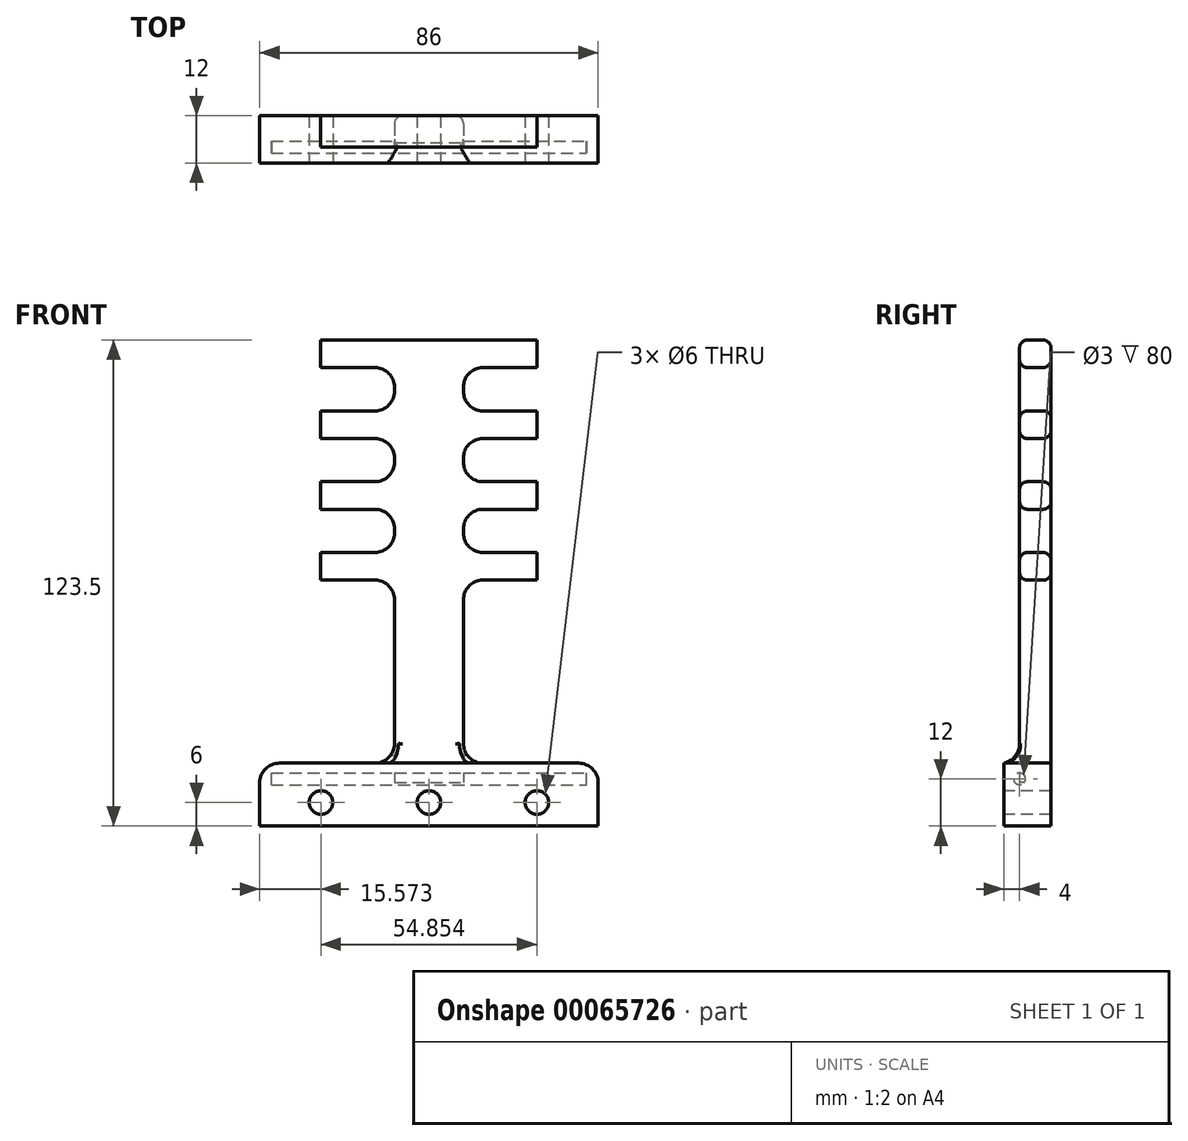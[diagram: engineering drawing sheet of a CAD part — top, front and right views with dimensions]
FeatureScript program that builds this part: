
annotation { "Feature Type Name" : "Feature", "Feature Type Description" : "" }
export const myFeature = defineFeature(function(context is Context, id is Id, definition is map)
    precondition{}
    {
        {
            var Q0;
            Q0=qCreatedBy(makeId("Top.planeOp"),FACE);
            var sketch = newSketch(context, id + "F0", { "sketchPlane" : qUnion([Q0])});
            skPoint(sketch, "E0.rect.middle", {"position": v(0, 0) * mm});
            skLineSegment(sketch, "E1", {"start": v(0, 0) * mm, "end": v(0, 2) * mm});
            skLineSegment(sketch, "E2", {"start": v(0, 2) * mm, "end": v(12, 2) * mm, "construction": true});
            skCircle(sketch, "E3", {"center": v(12, 2) * mm, "radius": 3 * mm});
            skCircle(sketch, "E4", {"center": v(12, 2) * mm, "radius": 6 * mm});
            skCircle(sketch, "E5.MirrorC", {"center": v(-12, 2) * mm, "radius": 3 * mm});
            skCircle(sketch, "E6.MirrorC", {"center": v(-12, 2) * mm, "radius": 6 * mm});
            skPoint(sketch, "E7.rect.middle", {"position": v(0, 2) * mm});
            skLineSegment(sketch, "E8", {"start": v(35, -4) * mm, "end": v(20.22, -4) * mm});
            skLineSegment(sketch, "E9", {"start": v(35, 8) * mm, "end": v(-35, 8) * mm});
            skPoint(sketch, "E10.rect.middle", {"position": v(0, 8) * mm});
            skLineSegment(sketch, "E11", {"start": v(-35, 8) * mm, "end": v(35, 8) * mm});
            skLineSegment(sketch, "E12.trimOffspring", {"start": v(17.45, 4.5) * mm, "end": v(13.66, 4.5) * mm});
            skLineSegment(sketch, "E13.MirrorCS", {"start": v(19.85, 8) * mm, "end": v(20.22, 8) * mm});
            skLineSegment(sketch, "E14.trimOffspring", {"start": v(-20.22, -4) * mm, "end": v(-35, -4) * mm});
            skLineSegment(sketch, "E15.trimOffspring", {"start": v(19.85, -4) * mm, "end": v(-19.85, -4) * mm});
            skLineSegment(sketch, "E16", {"start": v(-19.85, -4) * mm, "end": v(-20.22, -4) * mm});
            skLineSegment(sketch, "E17", {"start": v(19.85, -4) * mm, "end": v(20.22, -4) * mm});
            skPoint(sketch, "E18.left.start.orphan", {"position": v(-19.85, 8) * mm});
            skPoint(sketch, "E19.start.orphan", {"position": v(-20.22, 8) * mm});
            skLineSegment(sketch, "E20.bottom", {"start": v(-35, 8) * mm, "end": v(-43, 8) * mm});
            skLineSegment(sketch, "E20.top", {"start": v(-35, -4) * mm, "end": v(-43, -4) * mm});
            skLineSegment(sketch, "E20.right", {"start": v(-43, 8) * mm, "end": v(-43, -4) * mm});
            skLineSegment(sketch, "E21.bottom", {"start": v(35, 8) * mm, "end": v(43, 8) * mm});
            skLineSegment(sketch, "E21.top", {"start": v(35, -4) * mm, "end": v(43, -4) * mm});
            skLineSegment(sketch, "E21.right", {"start": v(43, 8) * mm, "end": v(43, -4) * mm});
            skSolve(sketch);
        }
        {
            var Q0;
            {var subQ4=sQuery(id+"F0.wireOp",EDGE,"E10.rect.right");Q0=makeQuery(id+"F0.imprint","IMPRINT",FACE,{"disambiguationData":[TD([[makeQuery(id+"F0.imprint","IMPRINT",EDGE,{"derivedFrom":subQ4}),1.0]])]});}
            var Q1;
            {var subQ3=sQuery(id+"F0.wireOp",EDGE,"E18.right");Q1=makeQuery(id+"F0.imprint","IMPRINT",FACE,{"disambiguationData":[TD([[makeQuery(id+"F0.imprint","IMPRINT",EDGE,{"derivedFrom":subQ3}),-1.0]])]});}
            var Q2;
            {var subQ5=sQuery(id+"F0.wireOp",EDGE,"E18.left");Q2=makeQuery(id+"F0.imprint","IMPRINT",FACE,{"disambiguationData":[TD([[makeQuery(id+"F0.imprint","IMPRINT",EDGE,{"derivedFrom":subQ5}),1.0]])]});}
            var Q3;
            Q3=makeQuery(id+"F0.imprint","IMPRINT",FACE,{"disambiguationData":[TD([[makeQuery(id+"F0.imprint","IMPRINT",EDGE,{"derivedFrom":sQuery(id+"F0.wireOp",EDGE,"E5.MirrorC")}),1.0]])]});
            var Q4;
            Q4=makeQuery(id+"F0.imprint","IMPRINT",FACE,{"disambiguationData":[TD([[makeQuery(id+"F0.imprint","IMPRINT",EDGE,{"derivedFrom":sQuery(id+"F0.wireOp",EDGE,"E5.MirrorC")}),-1.0]])]});
            var Q5;
            {var subQ0=sQuery(id+"F0.wireOp",EDGE,"E11");var subQ1=sQuery(id+"F0.wireOp",EDGE,"E4");var subQ2=makeQuery(id+"F0.imprint","INTERSECT",VERTEX,{"derivedFrom":[subQ1,subQ0]});Q5=makeQuery(id+"F0.imprint","IMPRINT",FACE,{"disambiguationData":[TD([[makeQuery(id+"F0.imprint","IMPRINT",EDGE,{"disambiguationData":[TD([[subQ2,-1.0]])],"derivedFrom":subQ1}),-1.0]])]});}
            var Q6;
            Q6=makeQuery(id+"F0.imprint","IMPRINT",FACE,{"disambiguationData":[TD([[makeQuery(id+"F0.imprint","IMPRINT",EDGE,{"derivedFrom":sQuery(id+"F0.wireOp",EDGE,"E3")}),-1.0]])]});
            var Q7;
            Q7=makeQuery(id+"F0.imprint","IMPRINT",FACE,{"disambiguationData":[TD([[makeQuery(id+"F0.imprint","IMPRINT",EDGE,{"derivedFrom":sQuery(id+"F0.wireOp",EDGE,"E3")}),1.0]])]});
            var Q8;
            {var subQ0=sQuery(id+"F0.wireOp",EDGE,"7a62f623-bed4-47ff-af37-e2dce5c890c03.MirrorCS");Q8=makeQuery(id+"F0.imprint","IMPRINT",FACE,{"disambiguationData":[TD([[makeQuery(id+"F0.imprint","IMPRINT",EDGE,{"derivedFrom":subQ0}),-1.0]])]});}
            var Q9;
            {var subQ4=sQuery(id+"F0.wireOp",EDGE,"E8");Q9=makeQuery(id+"F0.imprint","IMPRINT",FACE,{"disambiguationData":[TD([[makeQuery(id+"F0.imprint","IMPRINT",EDGE,{"derivedFrom":subQ4}),-1.0]])]});}
            var Q10;
            {var subQ3=sQuery(id+"F0.wireOp",EDGE,"E10.rect.top");Q10=makeQuery(id+"F0.imprint","IMPRINT",FACE,{"disambiguationData":[TD([[makeQuery(id+"F0.imprint","IMPRINT",EDGE,{"derivedFrom":subQ3}),-1.0]])]});}
            var Q11;
            Q11=makeQuery(id+"F0.imprint","IMPRINT",FACE,{"disambiguationData":[TD([[makeQuery(id+"F0.imprint","IMPRINT",EDGE,{"derivedFrom":sQuery(id+"F0.wireOp",EDGE,"NbMli8i6-iFg7-sWmi-01Ci-sI5fGouLRfiF")}),-1.0]])]});
            var Q12;
            {var subQ0=sQuery(id+"F0.wireOp",EDGE,"E19");Q12=makeQuery(id+"F0.imprint","IMPRINT",FACE,{"disambiguationData":[TD([[makeQuery(id+"F0.imprint","IMPRINT",EDGE,{"derivedFrom":subQ0}),1.0]])]});}
            var Q13;
            {var subQ1=sQuery(id+"F0.wireOp",EDGE,"E7.rect.left");Q13=makeQuery(id+"F0.imprint","IMPRINT",FACE,{"disambiguationData":[TD([[makeQuery(id+"F0.imprint","IMPRINT",EDGE,{"derivedFrom":subQ1}),-1.0]])]});}
            var Q14;
            Q14=makeQuery(id+"F0.imprint","IMPRINT",FACE,{"disambiguationData":[TD([[makeQuery(id+"F0.imprint","IMPRINT",EDGE,{"derivedFrom":sQuery(id+"F0.wireOp",EDGE,"E14.trimOffspring")}),-1.0]])]});
            extrude(context, id + "F1", {"entities" : qUnion([Q0, Q1, Q2, Q3, Q4, Q5, Q6, Q7, Q8, Q9, Q10, Q11, Q12, Q13, Q14]), "depth" : 16 * mm});
        }
        {
            var Q0;
            Q0=qCreatedBy(makeId("Front.planeOp"),FACE);
            var sketch = newSketch(context, id + "F2", { "sketchPlane" : qUnion([Q0])});
            skLineSegment(sketch, "E22", {"start": v(0, 0) * mm, "end": v(0, 12) * mm});
            skLineSegment(sketch, "E23", {"start": v(0, 6) * mm, "end": v(-27.43, 6) * mm, "construction": true});
            skCircle(sketch, "E24", {"center": v(-27.43, 6) * mm, "radius": 3 * mm});
            skCircle(sketch, "E25.MirrorC", {"center": v(27.43, 6) * mm, "radius": 3 * mm});
            skLineSegment(sketch, "E26", {"start": v(0, 6) * mm, "end": v(52.55, 6) * mm, "construction": true});
            skLineSegment(sketch, "E27", {"start": v(0, 0) * mm, "end": v(-52.55, 0) * mm, "construction": true});
            skLineSegment(sketch, "E28", {"start": v(-52.55, 0) * mm, "end": v(-52.55, 5) * mm, "construction": true});
            skLineSegment(sketch, "E29", {"start": v(-52.55, 7.5) * mm, "end": v(-52.55, 5) * mm, "construction": true});
            skCircle(sketch, "E30", {"center": v(-52.55, 7.5) * mm, "radius": 2.5 * mm});
            skCircle(sketch, "E31.MirrorC", {"center": v(52.55, 7.5) * mm, "radius": 2.5 * mm});
            skCircle(sketch, "E32", {"center": v(0, 6) * mm, "radius": 3 * mm});
            skSolve(sketch);
        }
        {
            var Q0;
            Q0=qSketchRegion(id+"F2",true);
            extrude(context, id + "F3", {"entities" : qUnion([Q0]), "operationType" : NewBodyOperationType.REMOVE, "oppositeDirection" : true, "depth" : 25 * mm, "symmetric" : true});
        }
        {
            var Q0;
            Q0=qCreatedBy(makeId("Right.planeOp"),FACE);
            var sketch = newSketch(context, id + "F4", { "sketchPlane" : qUnion([Q0])});
            skLineSegment(sketch, "E33", {"start": v(0, 0) * mm, "end": v(0, 12) * mm});
            skCircle(sketch, "E34", {"center": v(0, 12) * mm, "radius": 1.5 * mm});
            skSolve(sketch);
        }
        {
            var Q0;
            Q0=qSketchRegion(id+"F4",true);
            extrude(context, id + "F5", {"entities" : qUnion([Q0]), "operationType" : NewBodyOperationType.REMOVE, "oppositeDirection" : true, "depth" : 80 * mm, "symmetric" : true});
        }
        {
            var Q0;
            Q0=qCreatedBy(makeId("Front.planeOp"),FACE);
            var sketch = newSketch(context, id + "F6", { "sketchPlane" : qUnion([Q0])});
            skLineSegment(sketch, "E35.left", {"start": v(8.75, 111.5) * mm, "end": v(8.75, 110.5) * mm});
            skLineSegment(sketch, "E35.right", {"start": v(-8.75, 111.5) * mm, "end": v(-8.75, 110.5) * mm});
            skPoint(sketch, "E35.middle", {"position": v(0, 0) * mm});
            skLineSegment(sketch, "E36.bottom", {"start": v(27.5, 116.5) * mm, "end": v(13.75, 116.5) * mm});
            skLineSegment(sketch, "E36.top", {"start": v(27.5, 123.5) * mm, "end": v(-27.5, 123.5) * mm});
            skLineSegment(sketch, "E36.left", {"start": v(27.5, 116.5) * mm, "end": v(27.5, 123.5) * mm});
            skLineSegment(sketch, "E36.right", {"start": v(-27.5, 116.5) * mm, "end": v(-27.5, 123.5) * mm});
            skPoint(sketch, "E36.middle", {"position": v(0, 120) * mm});
            skLineSegment(sketch, "E37", {"start": v(0, 120) * mm, "end": v(0, 102) * mm, "construction": true});
            skLineSegment(sketch, "E38", {"start": v(0, 102) * mm, "end": v(0, 84) * mm, "construction": true});
            skLineSegment(sketch, "E39", {"start": v(0, 84) * mm, "end": v(0, 66) * mm, "construction": true});
            skLineSegment(sketch, "E40.bottom", {"start": v(27.5, 105.5) * mm, "end": v(13.75, 105.5) * mm});
            skLineSegment(sketch, "E40.top", {"start": v(27.5, 98.5) * mm, "end": v(13.75, 98.5) * mm});
            skLineSegment(sketch, "E40.left", {"start": v(27.5, 105.5) * mm, "end": v(27.5, 98.5) * mm});
            skLineSegment(sketch, "E40.right", {"start": v(-27.5, 105.5) * mm, "end": v(-27.5, 98.5) * mm});
            skPoint(sketch, "E40.middle", {"position": v(0, 102) * mm});
            skLineSegment(sketch, "E41.bottom", {"start": v(-27.5, 87.5) * mm, "end": v(-13.75, 87.5) * mm});
            skLineSegment(sketch, "E41.top", {"start": v(-27.5, 80.5) * mm, "end": v(-13.75, 80.5) * mm});
            skLineSegment(sketch, "E41.left", {"start": v(-27.5, 87.5) * mm, "end": v(-27.5, 80.5) * mm});
            skLineSegment(sketch, "E41.right", {"start": v(27.5, 87.5) * mm, "end": v(27.5, 80.5) * mm});
            skPoint(sketch, "E41.middle", {"position": v(0, 84) * mm});
            skLineSegment(sketch, "E42.bottom", {"start": v(-27.5, 69.5) * mm, "end": v(-13.75, 69.5) * mm});
            skLineSegment(sketch, "E42.top", {"start": v(-27.5, 62.5) * mm, "end": v(-13.75, 62.5) * mm});
            skLineSegment(sketch, "E42.left", {"start": v(-27.5, 69.5) * mm, "end": v(-27.5, 62.5) * mm});
            skLineSegment(sketch, "E42.right", {"start": v(27.5, 69.5) * mm, "end": v(27.5, 62.5) * mm});
            skPoint(sketch, "E42.middle", {"position": v(0, 66) * mm});
            skLineSegment(sketch, "E43.trimOffspring", {"start": v(13.75, 62.5) * mm, "end": v(27.5, 62.5) * mm});
            skLineSegment(sketch, "E44.trimOffspring", {"start": v(8.75, 57.5) * mm, "end": v(8.75, 11.04) * mm});
            skLineSegment(sketch, "E45.trimOffspring", {"start": v(13.75, 69.5) * mm, "end": v(27.5, 69.5) * mm});
            skLineSegment(sketch, "E46.trimOffspring", {"start": v(-8.75, 57.5) * mm, "end": v(-8.75, 11.04) * mm});
            skLineSegment(sketch, "E47.trimOffspring", {"start": v(13.75, 80.5) * mm, "end": v(27.5, 80.5) * mm});
            skLineSegment(sketch, "E48.trimOffspring", {"start": v(-8.75, 75.5) * mm, "end": v(-8.75, 74.5) * mm});
            skLineSegment(sketch, "E49.trimOffspring", {"start": v(8.75, 75.5) * mm, "end": v(8.75, 74.5) * mm});
            skLineSegment(sketch, "E50.trimOffspring", {"start": v(13.75, 87.5) * mm, "end": v(27.5, 87.5) * mm});
            skLineSegment(sketch, "E51.trimOffspring", {"start": v(-13.75, 98.5) * mm, "end": v(-27.5, 98.5) * mm});
            skLineSegment(sketch, "E52.trimOffspring", {"start": v(8.75, 93.5) * mm, "end": v(8.75, 92.5) * mm});
            skLineSegment(sketch, "E53.trimOffspring", {"start": v(-8.75, 93.5) * mm, "end": v(-8.75, 92.5) * mm});
            skLineSegment(sketch, "E54.trimOffspring", {"start": v(-13.75, 105.5) * mm, "end": v(-27.5, 105.5) * mm});
            skLineSegment(sketch, "E55.trimOffspring", {"start": v(-13.75, 116.5) * mm, "end": v(-27.5, 116.5) * mm});
            skPoint(sketch, "E56.orphan", {"position": v(-8.75, 120) * mm});
            skPoint(sketch, "E57.orphan", {"position": v(8.75, 120) * mm});
            skPoint(sketch, "E58.visualSharp", {"position": v(-8.75, 62.5) * mm});
            skArc(sketch, "E58.filletArc", {"start": v(-8.75, 57.5) * mm, "mid": v(-10.21, 61.04) * mm, "end": v(-13.75, 62.5) * mm});
            skPoint(sketch, "E59.visualSharp", {"position": v(8.75, 62.5) * mm});
            skArc(sketch, "E59.filletArc", {"start": v(13.75, 62.5) * mm, "mid": v(10.21, 61.04) * mm, "end": v(8.75, 57.5) * mm});
            skPoint(sketch, "E60.visualSharp", {"position": v(8.75, 69.5) * mm});
            skArc(sketch, "E60.filletArc", {"start": v(8.75, 74.5) * mm, "mid": v(10.21, 70.96) * mm, "end": v(13.75, 69.5) * mm});
            skPoint(sketch, "E61.visualSharp", {"position": v(8.75, 80.5) * mm});
            skArc(sketch, "E61.filletArc", {"start": v(13.75, 80.5) * mm, "mid": v(10.21, 79.04) * mm, "end": v(8.75, 75.5) * mm});
            skPoint(sketch, "E62.visualSharp", {"position": v(8.75, 87.5) * mm});
            skArc(sketch, "E62.filletArc", {"start": v(8.75, 92.5) * mm, "mid": v(10.21, 88.96) * mm, "end": v(13.75, 87.5) * mm});
            skPoint(sketch, "E63.visualSharp", {"position": v(8.75, 98.5) * mm});
            skArc(sketch, "E63.filletArc", {"start": v(13.75, 98.5) * mm, "mid": v(10.21, 97.04) * mm, "end": v(8.75, 93.5) * mm});
            skPoint(sketch, "E64.visualSharp", {"position": v(8.75, 105.5) * mm});
            skArc(sketch, "E64.filletArc", {"start": v(8.75, 110.5) * mm, "mid": v(10.21, 106.96) * mm, "end": v(13.75, 105.5) * mm});
            skPoint(sketch, "E65.visualSharp", {"position": v(8.75, 116.5) * mm});
            skArc(sketch, "E65.filletArc", {"start": v(13.75, 116.5) * mm, "mid": v(10.21, 115.04) * mm, "end": v(8.75, 111.5) * mm});
            skPoint(sketch, "E66.visualSharp", {"position": v(-8.75, 116.5) * mm});
            skArc(sketch, "E66.filletArc", {"start": v(-8.75, 111.5) * mm, "mid": v(-10.21, 115.04) * mm, "end": v(-13.75, 116.5) * mm});
            skPoint(sketch, "E67.visualSharp", {"position": v(-8.75, 105.5) * mm});
            skArc(sketch, "E67.filletArc", {"start": v(-13.75, 105.5) * mm, "mid": v(-10.21, 106.96) * mm, "end": v(-8.75, 110.5) * mm});
            skPoint(sketch, "E68.visualSharp", {"position": v(-8.75, 98.5) * mm});
            skArc(sketch, "E68.filletArc", {"start": v(-8.75, 93.5) * mm, "mid": v(-10.21, 97.04) * mm, "end": v(-13.75, 98.5) * mm});
            skPoint(sketch, "E69.visualSharp", {"position": v(-8.75, 87.5) * mm});
            skArc(sketch, "E69.filletArc", {"start": v(-13.75, 87.5) * mm, "mid": v(-10.21, 88.96) * mm, "end": v(-8.75, 92.5) * mm});
            skPoint(sketch, "E70.visualSharp", {"position": v(-8.75, 80.5) * mm});
            skArc(sketch, "E70.filletArc", {"start": v(-8.75, 75.5) * mm, "mid": v(-10.21, 79.04) * mm, "end": v(-13.75, 80.5) * mm});
            skPoint(sketch, "E71.visualSharp", {"position": v(-8.75, 69.5) * mm});
            skArc(sketch, "E71.filletArc", {"start": v(-13.75, 69.5) * mm, "mid": v(-10.21, 70.96) * mm, "end": v(-8.75, 74.5) * mm});
            skPoint(sketch, "E35.top.end.orphan", {"position": v(-8.75, -120) * mm});
            skPoint(sketch, "E35.top.start.orphan", {"position": v(8.75, -120) * mm});
            skLineSegment(sketch, "E72", {"start": v(8.75, 11.04) * mm, "end": v(-8.75, 11.04) * mm});
            skPoint(sketch, "E73.orphan", {"position": v(8.75, 0) * mm});
            skSolve(sketch);
        }
        {
            var Q0;
            Q0 = qSketchRegion(id + "F6", true);
            var Q1;
            Q1=makeQuery(id+"F1.opExtrude","SWEPT_FACE",FACE,{"disambiguationData":[OSD([sQuery(id+"F0.wireOp",EDGE,"E11"),sQuery(id+"F0.wireOp",EDGE,"E13.MirrorCS"),sQuery(id+"F0.wireOp",EDGE,"E20.bottom"),sQuery(id+"F0.wireOp",EDGE,"E21.bottom")])]});
            extrude(context, id + "F7", {"entities" : qUnion([Q0]), "operationType" : NewBodyOperationType.ADD, "endBound" : BoundingType.UP_TO_SURFACE, "oppositeDirection" : true, "endBoundEntityFace" : qUnion([Q1]), "depth" : 10 * mm});
        }
        {
            var Q0;
            Q0=makeQuery(id+"F7.opExtrude","CAP_EDGE",EDGE,{"disambiguationData":[OSD([sQuery(id+"F6.wireOp",EDGE,"E54.trimOffspring")])],"isStart":false});
            var Q1;
            Q1=makeQuery(id+"F7.opExtrude","CAP_EDGE",EDGE,{"disambiguationData":[OSD([sQuery(id+"F6.wireOp",EDGE,"E41.bottom")])],"isStart":false});
            var Q2;
            Q2=makeQuery(id+"F7.opExtrude","CAP_EDGE",EDGE,{"disambiguationData":[OSD([sQuery(id+"F6.wireOp",EDGE,"E42.bottom")])],"isStart":false});
            var Q3;
            Q3=makeQuery(id+"F7.opExtrude","CAP_EDGE",EDGE,{"disambiguationData":[OSD([sQuery(id+"F6.wireOp",EDGE,"E45.trimOffspring")])],"isStart":false});
            var Q4;
            Q4=makeQuery(id+"F7.opExtrude","CAP_EDGE",EDGE,{"disambiguationData":[OSD([sQuery(id+"F6.wireOp",EDGE,"E50.trimOffspring")])],"isStart":false});
            var Q5;
            Q5=makeQuery(id+"F7.opExtrude","CAP_EDGE",EDGE,{"disambiguationData":[OSD([sQuery(id+"F6.wireOp",EDGE,"E40.bottom")])],"isStart":false});
            var Q6;
            Q6=makeQuery(id+"F7.opExtrude","CAP_EDGE",EDGE,{"disambiguationData":[OSD([sQuery(id+"F6.wireOp",EDGE,"E36.top")])],"isStart":false});
            var Q7;
            Q7=makeQuery(id+"F7.opExtrude","CAP_EDGE",EDGE,{"disambiguationData":[OSD([sQuery(id+"F6.wireOp",EDGE,"E36.top")])],"isStart":true});
            var Q8;
            Q8=makeQuery(id+"F7.opExtrude","CAP_EDGE",EDGE,{"disambiguationData":[OSD([sQuery(id+"F6.wireOp",EDGE,"E44.trimOffspring")])],"isStart":false});
            var Q9;
            Q9=makeQuery(id+"F7.opExtrude","CAP_EDGE",EDGE,{"disambiguationData":[OSD([sQuery(id+"F6.wireOp",EDGE,"E46.trimOffspring")])],"isStart":false});
            var Q10;
            {var subQ0=sQuery(id+"F6.wireOp",EDGE,"E59.filletArc");var subQ1=sQuery(id+"F6.wireOp",EDGE,"E44.trimOffspring");Q10=makeQuery(id+"F7.boolean.opBoolean","SPLIT",EDGE,{"disambiguationData":[TD([makeQuery(id+"F7.opExtrude","SWEPT_FACE",FACE,{"disambiguationData":[OSD([subQ0])]})])],"derivedFrom":makeQuery(id+"F7.opExtrude","CAP_EDGE",EDGE,{"disambiguationData":[OSD([subQ1])],"isStart":true})});}
            var Q11;
            {var subQ0=sQuery(id+"F6.wireOp",EDGE,"E58.filletArc");var subQ1=sQuery(id+"F6.wireOp",EDGE,"E46.trimOffspring");Q11=makeQuery(id+"F7.boolean.opBoolean","SPLIT",EDGE,{"disambiguationData":[TD([makeQuery(id+"F7.opExtrude","SWEPT_FACE",FACE,{"disambiguationData":[OSD([subQ0])]})])],"derivedFrom":makeQuery(id+"F7.opExtrude","CAP_EDGE",EDGE,{"disambiguationData":[OSD([subQ1])],"isStart":true})});}
            var Q12;
            Q12=makeQuery(id+"F7.opExtrude","CAP_EDGE",EDGE,{"disambiguationData":[OSD([sQuery(id+"F6.wireOp",EDGE,"E45.trimOffspring")])],"isStart":true});
            var Q13;
            Q13=makeQuery(id+"F7.opExtrude","CAP_EDGE",EDGE,{"disambiguationData":[OSD([sQuery(id+"F6.wireOp",EDGE,"E50.trimOffspring")])],"isStart":true});
            var Q14;
            Q14=makeQuery(id+"F7.opExtrude","CAP_EDGE",EDGE,{"disambiguationData":[OSD([sQuery(id+"F6.wireOp",EDGE,"E40.bottom")])],"isStart":true});
            var Q15;
            Q15=makeQuery(id+"F7.opExtrude","CAP_EDGE",EDGE,{"disambiguationData":[OSD([sQuery(id+"F6.wireOp",EDGE,"E55.trimOffspring")])],"isStart":true});
            var Q16;
            Q16=makeQuery(id+"F7.opExtrude","CAP_EDGE",EDGE,{"disambiguationData":[OSD([sQuery(id+"F6.wireOp",EDGE,"E51.trimOffspring")])],"isStart":true});
            var Q17;
            Q17=makeQuery(id+"F7.opExtrude","CAP_EDGE",EDGE,{"disambiguationData":[OSD([sQuery(id+"F6.wireOp",EDGE,"E41.top")])],"isStart":true});
            fillet(context, id + "F8", {"entities" : qUnion([Q0, Q1, Q2, Q3, Q4, Q5, Q6, Q7, Q8, Q9, Q10, Q11, Q12, Q13, Q14, Q15, Q16, Q17]), "radius" : 2 * mm, "tangentPropagation" : true, "allowEdgeOverflow" : false});
        }
        {
            var Q0;
            Q0=makeQuery(id+"F7.boolean.opBoolean","INTERSECT",EDGE,{"derivedFrom":[makeQuery(id+"F1.opExtrude","CAP_FACE",FACE,{"disambiguationData":[OSD([sQuery(id+"F0.wireOp",EDGE,"E8"),sQuery(id+"F0.wireOp",EDGE,"E11"),sQuery(id+"F0.wireOp",EDGE,"E13.MirrorCS"),sQuery(id+"F0.wireOp",EDGE,"E14.trimOffspring"),sQuery(id+"F0.wireOp",EDGE,"E15.trimOffspring"),sQuery(id+"F0.wireOp",EDGE,"E16"),sQuery(id+"F0.wireOp",EDGE,"E17"),sQuery(id+"F0.wireOp",EDGE,"E20.bottom"),sQuery(id+"F0.wireOp",EDGE,"E20.top"),sQuery(id+"F0.wireOp",EDGE,"E20.right"),sQuery(id+"F0.wireOp",EDGE,"E21.bottom"),sQuery(id+"F0.wireOp",EDGE,"E21.top"),sQuery(id+"F0.wireOp",EDGE,"E21.right")])],"isStart":false}),makeQuery(id+"F7.opExtrude","CAP_FACE",FACE,{"disambiguationData":[OSD([sQuery(id+"F6.wireOp",EDGE,"E35.left"),sQuery(id+"F6.wireOp",EDGE,"E35.right"),sQuery(id+"F6.wireOp",EDGE,"E36.bottom"),sQuery(id+"F6.wireOp",EDGE,"E36.top"),sQuery(id+"F6.wireOp",EDGE,"E36.left"),sQuery(id+"F6.wireOp",EDGE,"E36.right"),sQuery(id+"F6.wireOp",EDGE,"E40.bottom"),sQuery(id+"F6.wireOp",EDGE,"E40.top"),sQuery(id+"F6.wireOp",EDGE,"E40.left"),sQuery(id+"F6.wireOp",EDGE,"E40.right"),sQuery(id+"F6.wireOp",EDGE,"E41.bottom"),sQuery(id+"F6.wireOp",EDGE,"E41.top"),sQuery(id+"F6.wireOp",EDGE,"E41.left"),sQuery(id+"F6.wireOp",EDGE,"E41.right"),sQuery(id+"F6.wireOp",EDGE,"E42.bottom"),sQuery(id+"F6.wireOp",EDGE,"E42.top"),sQuery(id+"F6.wireOp",EDGE,"E42.left"),sQuery(id+"F6.wireOp",EDGE,"E42.right"),sQuery(id+"F6.wireOp",EDGE,"E43.trimOffspring"),sQuery(id+"F6.wireOp",EDGE,"E44.trimOffspring"),sQuery(id+"F6.wireOp",EDGE,"E45.trimOffspring"),sQuery(id+"F6.wireOp",EDGE,"E46.trimOffspring"),sQuery(id+"F6.wireOp",EDGE,"E47.trimOffspring"),sQuery(id+"F6.wireOp",EDGE,"E48.trimOffspring"),sQuery(id+"F6.wireOp",EDGE,"E49.trimOffspring"),sQuery(id+"F6.wireOp",EDGE,"E50.trimOffspring"),sQuery(id+"F6.wireOp",EDGE,"E51.trimOffspring"),sQuery(id+"F6.wireOp",EDGE,"E52.trimOffspring"),sQuery(id+"F6.wireOp",EDGE,"E53.trimOffspring"),sQuery(id+"F6.wireOp",EDGE,"E54.trimOffspring"),sQuery(id+"F6.wireOp",EDGE,"E55.trimOffspring"),sQuery(id+"F6.wireOp",EDGE,"E58.filletArc"),sQuery(id+"F6.wireOp",EDGE,"E59.filletArc"),sQuery(id+"F6.wireOp",EDGE,"E60.filletArc"),sQuery(id+"F6.wireOp",EDGE,"E61.filletArc"),sQuery(id+"F6.wireOp",EDGE,"E62.filletArc"),sQuery(id+"F6.wireOp",EDGE,"E63.filletArc"),sQuery(id+"F6.wireOp",EDGE,"E64.filletArc"),sQuery(id+"F6.wireOp",EDGE,"E65.filletArc"),sQuery(id+"F6.wireOp",EDGE,"E66.filletArc"),sQuery(id+"F6.wireOp",EDGE,"E67.filletArc"),sQuery(id+"F6.wireOp",EDGE,"E68.filletArc"),sQuery(id+"F6.wireOp",EDGE,"E69.filletArc"),sQuery(id+"F6.wireOp",EDGE,"E70.filletArc"),sQuery(id+"F6.wireOp",EDGE,"E71.filletArc"),sQuery(id+"F6.wireOp",EDGE,"E72")])],"isStart":true})]});
            var Q1;
            Q1=makeQuery(id+"F1.opExtrude","CAP_EDGE",EDGE,{"disambiguationData":[OSD([sQuery(id+"F0.wireOp",EDGE,"E21.right")])],"isStart":false});
            var Q2;
            Q2=makeQuery(id+"F1.opExtrude","CAP_EDGE",EDGE,{"disambiguationData":[OSD([sQuery(id+"F0.wireOp",EDGE,"E20.right")])],"isStart":false});
            fillet(context, id + "F9", {"entities" : qUnion([Q0, Q1, Q2]), "radius" : 5 * mm, "tangentPropagation" : true, "allowEdgeOverflow" : false});
        }
    });
